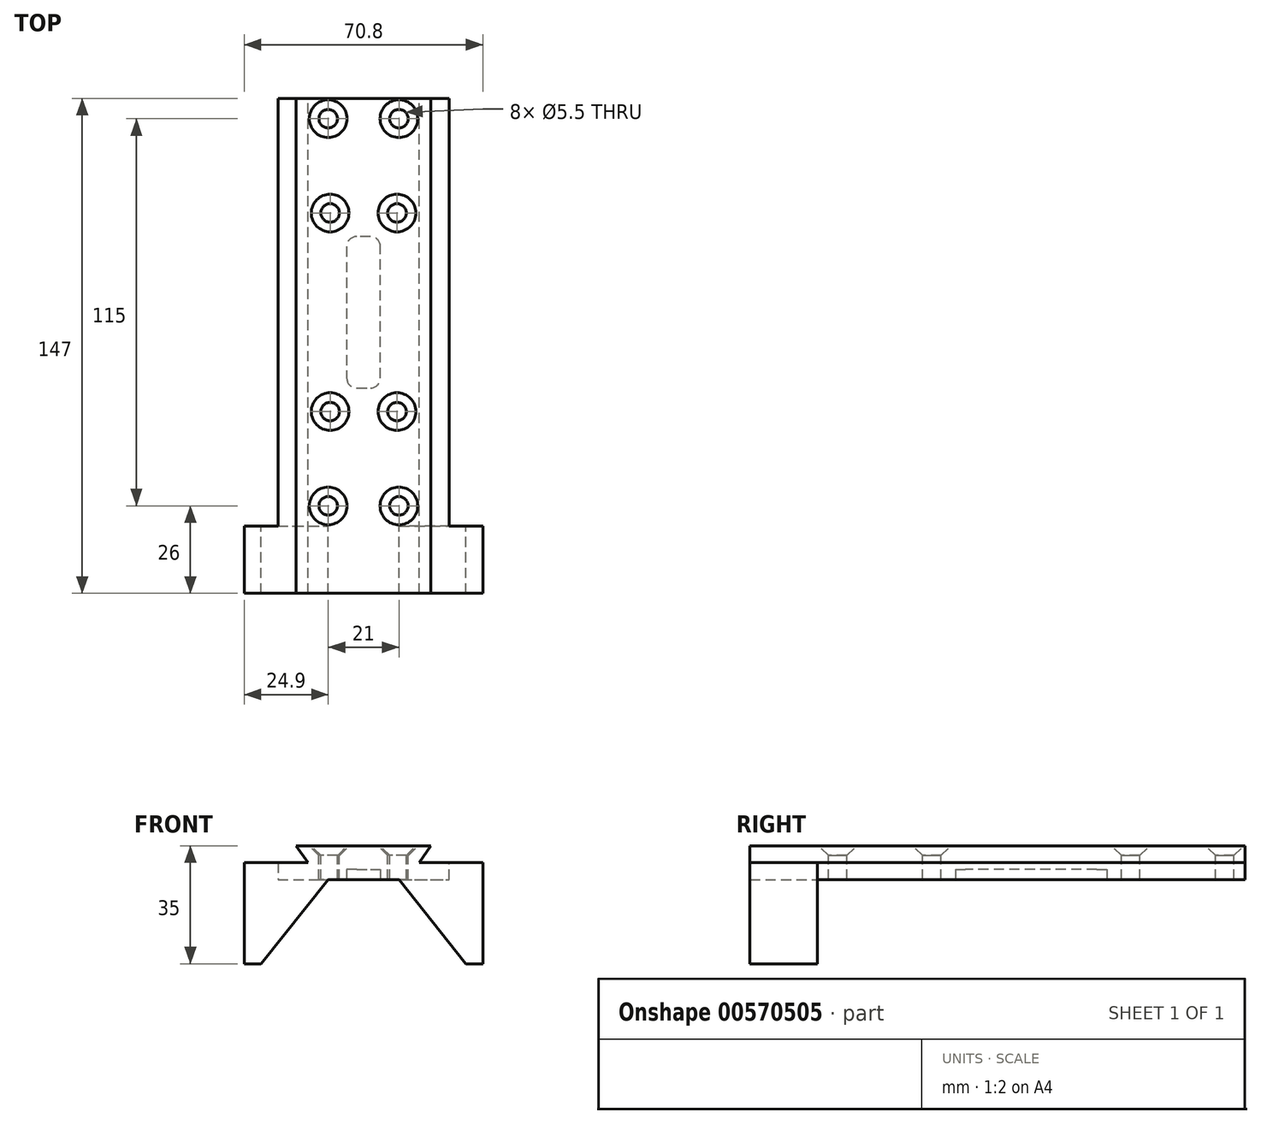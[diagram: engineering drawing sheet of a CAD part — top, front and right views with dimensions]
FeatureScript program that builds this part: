
annotation { "Feature Type Name" : "Feature", "Feature Type Description" : "" }
export const myFeature = defineFeature(function(context is Context, id is Id, definition is map)
    precondition{}
    {
        {
            var Q0;
            Q0=qCreatedBy(makeId("Front.planeOp"),FACE);
            var sketch = newSketch(context, id + "F0", { "sketchPlane" : qUnion([Q0])});
            skLineSegment(sketch, "E0", {"start": v(-25.4, 0) * mm, "end": v(25.4, 0) * mm});
            skLineSegment(sketch, "E1", {"start": v(25.4, 0) * mm, "end": v(25.4, 5) * mm});
            skLineSegment(sketch, "E2", {"start": v(25.4, 5) * mm, "end": v(16.5, 5) * mm});
            skLineSegment(sketch, "E3", {"start": v(16.5, 5) * mm, "end": v(20, 10) * mm});
            skLineSegment(sketch, "E4", {"start": v(20, 10) * mm, "end": v(-20, 10) * mm});
            skLineSegment(sketch, "E5", {"start": v(-20, 10) * mm, "end": v(-16.5, 5) * mm});
            skLineSegment(sketch, "E6", {"start": v(-16.5, 5) * mm, "end": v(-25.4, 5) * mm});
            skLineSegment(sketch, "E7", {"start": v(-25.4, 5) * mm, "end": v(-25.4, 0) * mm});
            skSolve(sketch);
        }
        {
            var Q0;
            Q0=makeQuery(id+"F0.imprint","IMPRINT",FACE,{"disambiguationData":[TD([[makeQuery(id+"F0.imprint","IMPRINT",EDGE,{"derivedFrom":sQuery(id+"F0.wireOp",EDGE,"E0")}),1.0]])]});
            extrude(context, id + "F1", {"entities" : qUnion([Q0]), "depth" : 63.5 * mm, "offsetDistance" : 25 * mm, "hasSecondDirection" : true, "secondDirectionOppositeDirection" : true, "secondDirectionDepth" : 63.5 * mm});
        }
        {
            var Q0;
            Q0=makeQuery(id+"F1.opExtrude","SWEPT_FACE",FACE,{"disambiguationData":[OSD([sQuery(id+"F0.wireOp",EDGE,"E0")])]});
            var sketch = newSketch(context, id + "F2", { "sketchPlane" : qUnion([Q0])});
            skCircle(sketch, "E8", {"center": v(-10.5, 57.5) * mm, "radius": 2.15 * mm});
            skCircle(sketch, "E9", {"center": v(-9.93, 29.5) * mm, "radius": 2.15 * mm});
            skCircle(sketch, "E10.MirrorC", {"center": v(9.93, 29.5) * mm, "radius": 2.15 * mm});
            skCircle(sketch, "E11.MirrorC", {"center": v(10.5, 57.5) * mm, "radius": 2.15 * mm});
            skCircle(sketch, "E12.MirrorC", {"center": v(9.93, -29.5) * mm, "radius": 2.15 * mm});
            skCircle(sketch, "E13.MirrorC", {"center": v(10.5, -57.5) * mm, "radius": 2.15 * mm});
            skCircle(sketch, "E14.MirrorC", {"center": v(-10.5, -57.5) * mm, "radius": 2.15 * mm});
            skCircle(sketch, "E15.MirrorC", {"center": v(-9.93, -29.5) * mm, "radius": 2.15 * mm});
            skSolve(sketch);
        }
        {
            var Q0;
            Q0=makeQuery(id+"F1.opExtrude","SWEPT_FACE",FACE,{"disambiguationData":[OSD([sQuery(id+"F0.wireOp",EDGE,"E0")])]});
            var sketch = newSketch(context, id + "F3", { "sketchPlane" : qUnion([Q0])});
            skLineSegment(sketch, "E16", {"start": v(-2, 22.5) * mm, "end": v(2, 22.5) * mm});
            skLineSegment(sketch, "E17", {"start": v(5, 19.5) * mm, "end": v(5, -19.5) * mm});
            skLineSegment(sketch, "E18", {"start": v(2, -22.5) * mm, "end": v(-2, -22.5) * mm});
            skLineSegment(sketch, "E19", {"start": v(-5, -19.5) * mm, "end": v(-5, 19.5) * mm});
            skPoint(sketch, "E20.visualSharp", {"position": v(5, 22.5) * mm});
            skArc(sketch, "E20.filletArc", {"start": v(5, 19.5) * mm, "mid": v(4.12, 21.62) * mm, "end": v(2, 22.5) * mm});
            skPoint(sketch, "E21.visualSharp", {"position": v(-5, 22.5) * mm});
            skArc(sketch, "E21.filletArc", {"start": v(-2, 22.5) * mm, "mid": v(-4.12, 21.62) * mm, "end": v(-5, 19.5) * mm});
            skPoint(sketch, "E22.visualSharp", {"position": v(-5, -22.5) * mm});
            skArc(sketch, "E22.filletArc", {"start": v(-5, -19.5) * mm, "mid": v(-4.12, -21.62) * mm, "end": v(-2, -22.5) * mm});
            skPoint(sketch, "E23.visualSharp", {"position": v(5, -22.5) * mm});
            skArc(sketch, "E23.filletArc", {"start": v(2, -22.5) * mm, "mid": v(4.12, -21.62) * mm, "end": v(5, -19.5) * mm});
            skSolve(sketch);
        }
        {
            var Q0;
            Q0 = qSketchRegion(id + "F3", true);
            extrude(context, id + "F4", {"entities" : qUnion([Q0]), "operationType" : NewBodyOperationType.REMOVE, "oppositeDirection" : true, "depth" : 3 * mm, "offsetDistance" : 25 * mm});
        }
        {
            var Q0;
            Q0=makeQuery(id+"F1.opExtrude","SWEPT_FACE",FACE,{"disambiguationData":[OSD([sQuery(id+"F0.wireOp",EDGE,"E4")])]});
            var sketch = newSketch(context, id + "F5", { "sketchPlane" : qUnion([Q0])});
            skPoint(sketch, "E24", {"position": v(-10.5, 57.5) * mm});
            skPoint(sketch, "E25", {"position": v(10.5, 57.5) * mm});
            skPoint(sketch, "E26", {"position": v(9.93, 29.5) * mm});
            skPoint(sketch, "E27", {"position": v(-9.93, 29.5) * mm});
            skPoint(sketch, "E28", {"position": v(-9.93, -29.5) * mm});
            skPoint(sketch, "E29", {"position": v(9.93, -29.5) * mm});
            skPoint(sketch, "E30", {"position": v(10.5, -57.5) * mm});
            skPoint(sketch, "E31", {"position": v(-10.5, -57.5) * mm});
            skSolve(sketch);
        }
        {
            var Q0;
            Q0=sQuery(id+"F5.wireOp",VERTEX,"E24");
            var Q1;
            Q1=sQuery(id+"F5.wireOp",VERTEX,"E25");
            var Q2;
            Q2=sQuery(id+"F5.wireOp",VERTEX,"E27");
            var Q3;
            Q3=sQuery(id+"F5.wireOp",VERTEX,"E26");
            var Q4;
            Q4=sQuery(id+"F5.wireOp",VERTEX,"E28");
            var Q5;
            Q5=sQuery(id+"F5.wireOp",VERTEX,"E29");
            var Q6;
            Q6=sQuery(id+"F5.wireOp",VERTEX,"E31");
            var Q7;
            Q7=sQuery(id+"F5.wireOp",VERTEX,"E30");
            var Q8;
            Q8=makeQuery(id+"F1.opExtrude","SWEPT_BODY",BODY,{"disambiguationData":[OSD([sQuery(id+"F0.wireOp",EDGE,"E0"),sQuery(id+"F0.wireOp",EDGE,"E1"),sQuery(id+"F0.wireOp",EDGE,"E2"),sQuery(id+"F0.wireOp",EDGE,"E3"),sQuery(id+"F0.wireOp",EDGE,"E4"),sQuery(id+"F0.wireOp",EDGE,"E5"),sQuery(id+"F0.wireOp",EDGE,"E6"),sQuery(id+"F0.wireOp",EDGE,"E7")])]});
            hole(context, id + "F6", {"style" : HoleStyle.C_SINK, "endStyle" : HoleEndStyle.THROUGH, "standardTappedOrClearance" : lookupTablePath({ "standard" : "ISO", "fit" : "Normal", "size" : "M5", "type" : "Clearance" }), "standardBlindInLast" : lookupTablePath({ "fit" : "Standard", "standard" : "ISO", "size" : "M5", "type" : "Clearance" }), "holeDiameter" : 5.5 * mm, "cSinkDiameter" : 11.2 * mm, "cSinkAngle" : 90 * degree, "isTappedThrough" : true, "tappedDepth" : 12 * mm, "tapClearance" : 3, "startFromSketch" : true, "locations" : qUnion([Q0, Q1, Q2, Q3, Q4, Q5, Q6, Q7]), "scope" : qUnion([Q8])});
        }
        {
            var Q0;
            Q0=makeQuery(id+"F1.opExtrude","CAP_FACE",FACE,{"disambiguationData":[OSD([sQuery(id+"F0.wireOp",EDGE,"E0"),sQuery(id+"F0.wireOp",EDGE,"E1"),sQuery(id+"F0.wireOp",EDGE,"E2"),sQuery(id+"F0.wireOp",EDGE,"E3"),sQuery(id+"F0.wireOp",EDGE,"E4"),sQuery(id+"F0.wireOp",EDGE,"E5"),sQuery(id+"F0.wireOp",EDGE,"E6"),sQuery(id+"F0.wireOp",EDGE,"E7")])],"isStart":false});
            var sketch = newSketch(context, id + "F7", { "sketchPlane" : qUnion([Q0])});
            skLineSegment(sketch, "E32", {"start": v(25.4, 5) * mm, "end": v(35.4, 5) * mm});
            skLineSegment(sketch, "E33", {"start": v(35.4, 5) * mm, "end": v(35.4, -25) * mm});
            skLineSegment(sketch, "E34", {"start": v(35.4, -25) * mm, "end": v(30.4, -25) * mm});
            skLineSegment(sketch, "E35", {"start": v(30.4, -25) * mm, "end": v(10.57, 0) * mm});
            skLineSegment(sketch, "E36", {"start": v(10.57, 0) * mm, "end": v(0, 0) * mm});
            skLineSegment(sketch, "E37", {"start": v(0, 0) * mm, "end": v(0, 5) * mm});
            skLineSegment(sketch, "E38", {"start": v(25.4, 5) * mm, "end": v(0, 5) * mm});
            skLineSegment(sketch, "E39.MirrorCS", {"start": v(-25.4, 5) * mm, "end": v(0, 5) * mm});
            skLineSegment(sketch, "E40.MirrorCS", {"start": v(-10.57, 0) * mm, "end": v(0, 0) * mm});
            skLineSegment(sketch, "E41.MirrorCS", {"start": v(-30.4, -25) * mm, "end": v(-10.57, 0) * mm});
            skLineSegment(sketch, "E42.MirrorCS", {"start": v(-35.4, -25) * mm, "end": v(-30.4, -25) * mm});
            skLineSegment(sketch, "E43.MirrorCS", {"start": v(-35.4, 5) * mm, "end": v(-35.4, -25) * mm});
            skLineSegment(sketch, "E44.MirrorCS", {"start": v(-25.4, 5) * mm, "end": v(-35.4, 5) * mm});
            skSolve(sketch);
        }
        {
            var Q0;
            Q0 = qSketchRegion(id + "F7", true);
            extrude(context, id + "F8", {"entities" : qUnion([Q0]), "operationType" : NewBodyOperationType.ADD, "depth" : 20 * mm, "offsetDistance" : 25 * mm});
        }
        {
            var Q0;
            Q0=makeQuery(id+"F1.opExtrude","CAP_FACE",FACE,{"disambiguationData":[OSD([sQuery(id+"F0.wireOp",EDGE,"E0"),sQuery(id+"F0.wireOp",EDGE,"E1"),sQuery(id+"F0.wireOp",EDGE,"E2"),sQuery(id+"F0.wireOp",EDGE,"E3"),sQuery(id+"F0.wireOp",EDGE,"E4"),sQuery(id+"F0.wireOp",EDGE,"E5"),sQuery(id+"F0.wireOp",EDGE,"E6"),sQuery(id+"F0.wireOp",EDGE,"E7")])],"isStart":false});
            extrude(context, id + "F9", {"entities" : qUnion([Q0]), "operationType" : NewBodyOperationType.ADD, "depth" : 20 * mm, "offsetDistance" : 25 * mm});
        }
    });
